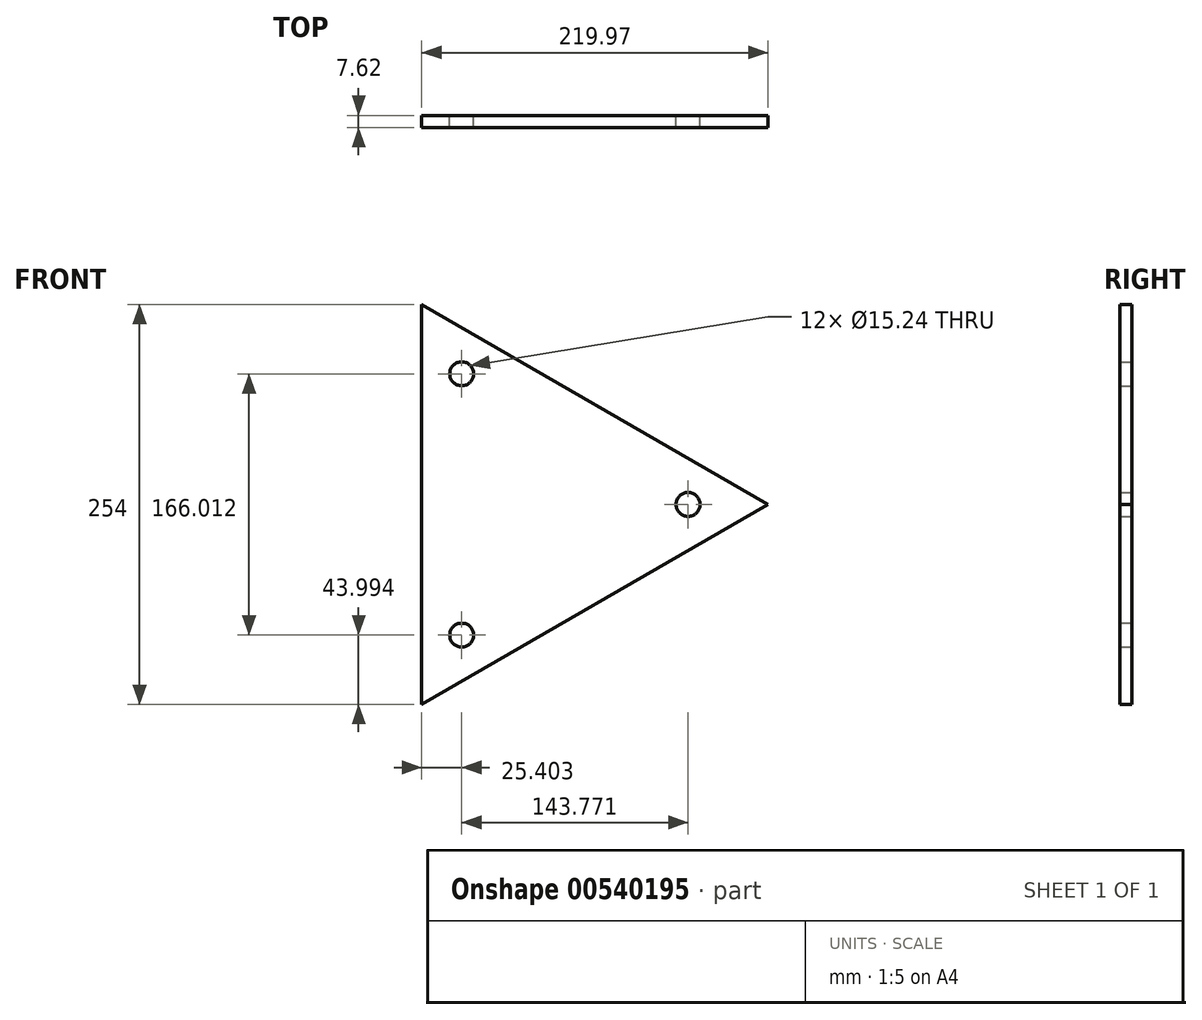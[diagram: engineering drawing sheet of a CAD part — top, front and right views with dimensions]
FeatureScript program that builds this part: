
annotation { "Feature Type Name" : "Feature", "Feature Type Description" : "" }
export const myFeature = defineFeature(function(context is Context, id is Id, definition is map)
    precondition{}
    {
        {
            var Q0;
            Q0=qCreatedBy(makeId("Front.planeOp"),FACE);
            var sketch = newSketch(context, id + "F0", { "sketchPlane" : qUnion([Q0])});
            skLineSegment(sketch, "E0", {"start": v(-294.68, 127) * mm, "end": v(-294.68, -127) * mm});
            skLineSegment(sketch, "E1", {"start": v(-294.68, -127) * mm, "end": v(-74.7, 0) * mm});
            skLineSegment(sketch, "E2", {"start": v(-74.7, 0) * mm, "end": v(-294.68, 127) * mm});
            skCircle(sketch, "E3", {"center": v(-269.28, 83) * mm, "radius": 7.62 * mm});
            skCircle(sketch, "E4", {"center": v(-125.5, 0) * mm, "radius": 7.62 * mm});
            skCircle(sketch, "E5", {"center": v(-269.28, -83) * mm, "radius": 7.62 * mm});
            skSolve(sketch);
        }
        {
            var Q0;
            Q0=makeQuery(id+"F0.imprint","IMPRINT",FACE,{"disambiguationData":[TD([[makeQuery(id+"F0.imprint","IMPRINT",EDGE,{"derivedFrom":sQuery(id+"F0.wireOp",EDGE,"E0")}),1.0]])]});
            extrude(context, id + "F1", {"entities" : qUnion([Q0]), "endBound" : BoundingType.SYMMETRIC, "depth" : 7.62 * mm, "offsetDistance" : 25.4 * mm});
        }
        {
            var Q0;
            Q0=makeQuery(id+"F0.imprint","IMPRINT",FACE,{"disambiguationData":[TD([[makeQuery(id+"F0.imprint","IMPRINT",EDGE,{"derivedFrom":sQuery(id+"F0.wireOp",EDGE,"E3")}),1.0]])]});
            var Q1;
            Q1=makeQuery(id+"F0.imprint","IMPRINT",FACE,{"disambiguationData":[TD([[makeQuery(id+"F0.imprint","IMPRINT",EDGE,{"derivedFrom":sQuery(id+"F0.wireOp",EDGE,"E4")}),1.0]])]});
            var Q2;
            Q2=makeQuery(id+"F0.imprint","IMPRINT",FACE,{"disambiguationData":[TD([[makeQuery(id+"F0.imprint","IMPRINT",EDGE,{"derivedFrom":sQuery(id+"F0.wireOp",EDGE,"E5")}),1.0]])]});
            extrude(context, id + "F2", {"entities" : qUnion([Q0, Q1, Q2]), "endBound" : BoundingType.SYMMETRIC, "depth" : 7.62 * mm, "offsetDistance" : 25.4 * mm});
        }
        {
            var Q0;
            Q0=makeQuery(id+"F2.opExtrude","SWEPT_BODY",BODY,{"disambiguationData":[OSD([sQuery(id+"F0.wireOp",EDGE,"E3")])]});
            var Q1;
            Q1=makeQuery(id+"F2.opExtrude","SWEPT_BODY",BODY,{"disambiguationData":[OSD([sQuery(id+"F0.wireOp",EDGE,"E4")])]});
            var Q2;
            Q2=makeQuery(id+"F2.opExtrude","SWEPT_BODY",BODY,{"disambiguationData":[OSD([sQuery(id+"F0.wireOp",EDGE,"E5")])]});
            var Q3;
            Q3=makeQuery(id+"F1.opExtrude","SWEPT_BODY",BODY,{"disambiguationData":[OSD([sQuery(id+"F0.wireOp",EDGE,"E0"),sQuery(id+"F0.wireOp",EDGE,"E1"),sQuery(id+"F0.wireOp",EDGE,"E2"),sQuery(id+"F0.wireOp",EDGE,"E3"),sQuery(id+"F0.wireOp",EDGE,"E4"),sQuery(id+"F0.wireOp",EDGE,"E5")])]});
            booleanBodies(context, id + "F3", {"operationType" : BooleanOperationType.SUBTRACTION, "tools" : qUnion([Q0, Q1, Q2]), "targets" : qUnion([Q3])});
        }
    });
